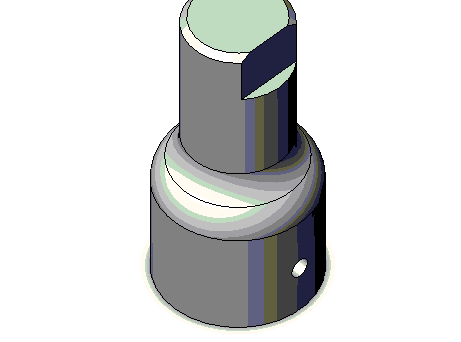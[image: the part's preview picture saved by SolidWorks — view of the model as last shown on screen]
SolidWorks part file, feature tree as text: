
SOLIDWORKS PART (.sldprt)
format: sldprt  version: not decoded by parser v0  size: 196,096 bytes
history: native  units: mm
features: sketch x5, cut_extrude x3, extrude x2, fillet x2, material x1, chamfer x1 (+14 scaffold rows collapsed)
feature tree (28):
  scaffold x14  (default folders/planes/origin — collapsed)
  material  "Material <sin especificar>"
  sketch  "Sketch1"  dims[D1=12.7mm]
  extrude  "Base-Extrude"  Depth=38.1mm
  sketch  "Sketch3"  dims[D1=3.175mm]
  extrude  "Boss-Extrude1"  Depth=15.875mm
  sketch  "Sketch4"  dims[D1=1.5875mm]
  cut_extrude  "Cut-Extrude1"  Depth=12.7mm
  fillet  "Fillet1"  Radius=4.7625mm
  fillet  "Fillet2"  Radius=4.7625mm
  sketch  "Sketch5"  dims[D2=~2.38125mm D1=6.35mm]
  cut_extrude  "Cut-Extrude2"  [1 undecoded]
  sketch  "Sketch7"
  cut_extrude  "Cut-Extrude3"  Depth=6.35mm
  chamfer  "Chamfer1"  Distance=0.79375mm Angle=45deg
decode coverage: 11 of 13 modeling features carry decoded parameters
note: ~ marks probable driven/reference dimensions
note: 1 parameter value undecoded
note: suppression state not decoded; provenance and decode notes live in map.json
